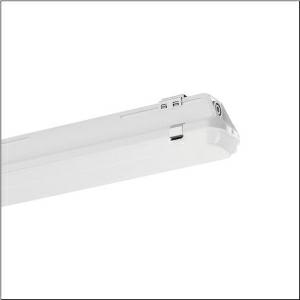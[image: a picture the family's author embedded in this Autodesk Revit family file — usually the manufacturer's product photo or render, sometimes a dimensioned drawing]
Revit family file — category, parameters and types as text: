
# Revit family: monsun_21_51fb10dl440k
name_source: partatom
category: Lighting Fixtures
units: mm (PartAtom-declared; Revit-internal decimal feet)

## family parameters
Cut with Voids When Loaded = No
Host = Face
Light Source = No
Part Type = Normal
Room Calculation Point = No
Round Connector Dimension = Use Diameter
Shared = No

## types (1)
- --- (1 x LED, 4330 lm, 24.3 W, 4000K)
    Apparent Load = 24 VA
    CIE Flux Codes = 46 76 93 94 100
    Color Rendering = 80
    Color Temperature = 4000K
    Default Elevation = 1800 mm
    Description = Monsun 21, damp-proof luminaire, chain hanger, primary optical cover: enclosure, of PMMA, light emission: direct distribution, primary light characteristic: symmetric, installation type: suspended mounting, surface-mounted, horizontal mounting, vertical mounting, LED, rated luminous flux: 4.330lm, luminous efficacy: 178lm/W, light colour: 840, colour temperature: 4000K, control gear: DALI 2, with terminal, 5-pole, max. 2.5mm², mains connection: 220..240V, AC, 50/60Hz, rated input power: 25W, housing, of glass-fibre reinforced plastic, uncoated, bright grey, incl. chain hanger, length: 1.299mm, width: 90mm, height: 88mm, clip for enclosure, of stainless steel (V2A), ceiling mounting element, of stainless steel (V2A), chain hanger, of stainless steel (V2A), protection rating (complete): IP66, insulation class (complete): insulation class I (protective earthing), certification: CE, ENEC, VDE, UKCA, protection symbol: D, impact resistance: IK04, permissible operating ambient temperature: -25..+35°C, standard: EN 50419, EN 60598-2-1, corresponds to IFS (International Featured Standards) requirements for safety and quality in the food industry, for indoor or canopied outdoor use, no direct snow, no direct sun, no direct rain, LABS conformity tested according to VDMA 24364:2018-05, contact your sales advisor before using the luminaires in applications with unclear chemical exposure, large temperature fluctuations or condensation-forming humidity, packaging unit: 1 piece
    Height = 88 mm
    Lamp = 1 x LED
    Lamp Light Flux = 4330 lm
    Lamp Power = 24.3 W
    Lamp count = 1
    Length = 1299 mm
    Luminous efficacy = 178 lm/W
    Manufacturer = Siteco
    ModVariant = No
    Model = 51FB10DL440K
    Mounting Place = Ceiling
    Mounting Type = Surface mounted
    Number of Poles = 1
    OnlyDefault = Yes
    Power Factor = 1
    Product Name = Monsun 21
    Product group = damp-proof luminaire
    ProductGroupID = 300
    Protection Class = Protection class I
    Protection Degree = IP 66
    RLX_Detail_Level = 1
    RLX_Emergency_Light_Flux = 0 lm
    RLX_Emergency_Type = 0
    RLX_Emergency_Type_DB = No
    RlxData = <blob elided: 93493 chars, md5=cbe080bd>
    Socket = socket
    Standby Power = 0 W
    System Light Flux = 4330 lm
    System Power = 24 W
    Type Comments = factory setting: luminous flux: 100 % | dim-lin: 254 | 164 mA
    Type Image = l_1319656.jpg
    URL = http://relux.com
    VarID = @adj_037307
    Voltage = 0 V
    Weight = 0.00 kg
    Width = 90 mm

## geometry (parser evidence)
native form markers: Blend x4, Sweep x11
no freeform markers — native parametric forms only
